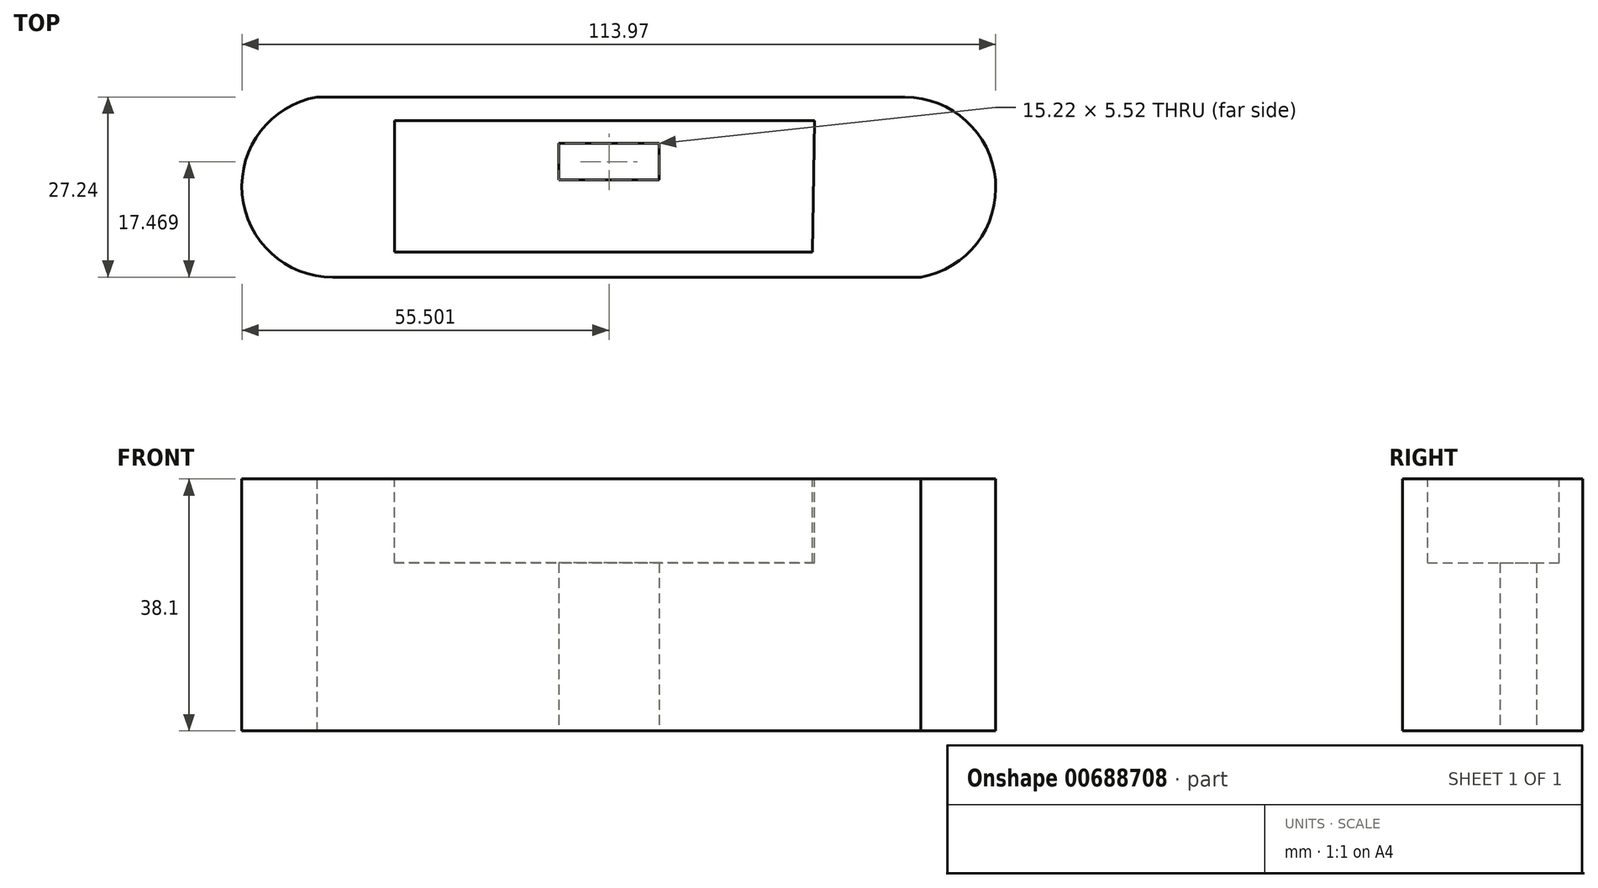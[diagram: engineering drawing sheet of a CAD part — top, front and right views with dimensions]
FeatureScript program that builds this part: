
annotation { "Feature Type Name" : "Feature", "Feature Type Description" : "" }
export const myFeature = defineFeature(function(context is Context, id is Id, definition is map)
    precondition{}
    {
        {
            var Q0;
            Q0=qCreatedBy(makeId("Top.planeOp"),FACE);
            var sketch = newSketch(context, id + "F0", { "sketchPlane" : qUnion([Q0])});
            skLineSegment(sketch, "E0", {"start": v(-44.14, 0) * mm, "end": v(44.76, 0) * mm});
            skArc(sketch, "E1", {"start": v(47.13, -27.24) * mm, "mid": v(58.43, -12.53) * mm, "end": v(44.76, 0) * mm});
            skLineSegment(sketch, "E2", {"start": v(47.13, -27.24) * mm, "end": v(-41.77, -27.24) * mm});
            skArc(sketch, "E3", {"start": v(-44.14, 0) * mm, "mid": v(-55.44, -14.71) * mm, "end": v(-41.77, -27.24) * mm});
            skSolve(sketch);
        }
        {
            var Q0;
            Q0=makeQuery(id+"F0.imprint","IMPRINT",FACE,{"disambiguationData":[TD([[makeQuery(id+"F0.imprint","IMPRINT",EDGE,{"derivedFrom":sQuery(id+"F0.wireOp",EDGE,"E0")}),-1.0]])]});
            extrude(context, id + "F1", {"entities" : qUnion([Q0]), "depth" : 12.7 * mm, "offsetDistance" : 25.4 * mm});
        }
        {
            var Q0;
            Q0=makeQuery(id+"F1.opExtrude","CAP_FACE",FACE,{"disambiguationData":[OSD([sQuery(id+"F0.wireOp",EDGE,"E0"),sQuery(id+"F0.wireOp",EDGE,"E1"),sQuery(id+"F0.wireOp",EDGE,"E2"),sQuery(id+"F0.wireOp",EDGE,"E3")])],"isStart":true});
            var sketch = newSketch(context, id + "F2", { "sketchPlane" : qUnion([Q0])});
            skLineSegment(sketch, "E4", {"start": v(-34.49, 27.24) * mm, "end": v(-34.49, 0) * mm});
            skSolve(sketch);
        }
        {
            var Q0;
            {var subQ0=sQuery(id+"F2.wireOp",EDGE,"E4");Q0=makeQuery(id+"F2.imprint","IMPRINT",FACE,{"disambiguationData":[TD([[makeQuery(id+"F2.imprint","IMPRINT",EDGE,{"derivedFrom":subQ0}),1.0]])]});}
            var sketch = newSketch(context, id + "F3", { "sketchPlane" : qUnion([Q0])});
            skLineSegment(sketch, "E5", {"start": v(31.5, 26.78) * mm, "end": v(31.5, 0) * mm});
            skSolve(sketch);
        }
        {
            var Q0;
            Q0 = qSketchRegion(id + "F3", true);
            var Q1;
            {var subQ0=sQuery(id+"F2.wireOp",EDGE,"E4");Q1=makeQuery(id+"F2.imprint","IMPRINT",FACE,{"disambiguationData":[TD([[makeQuery(id+"F2.imprint","IMPRINT",EDGE,{"derivedFrom":subQ0}),1.0]])]});}
            extrude(context, id + "F4", {"entities" : qUnion([Q0, Q1]), "operationType" : NewBodyOperationType.ADD, "depth" : 25.4 * mm, "offsetDistance" : 25.4 * mm});
        }
        {
            var Q0;
            Q0=makeQuery(id+"F1.opExtrude","CAP_FACE",FACE,{"disambiguationData":[OSD([sQuery(id+"F0.wireOp",EDGE,"E0"),sQuery(id+"F0.wireOp",EDGE,"E1"),sQuery(id+"F0.wireOp",EDGE,"E2"),sQuery(id+"F0.wireOp",EDGE,"E3")])],"isStart":true});
            extrude(context, id + "F5", {"entities" : qUnion([Q0]), "operationType" : NewBodyOperationType.ADD, "depth" : 25.4 * mm, "offsetDistance" : 25.4 * mm});
        }
        {
            var Q0;
            Q0=makeQuery(id+"F1.opExtrude","CAP_FACE",FACE,{"disambiguationData":[OSD([sQuery(id+"F0.wireOp",EDGE,"E0"),sQuery(id+"F0.wireOp",EDGE,"E1"),sQuery(id+"F0.wireOp",EDGE,"E2"),sQuery(id+"F0.wireOp",EDGE,"E3")])],"isStart":false});
            var sketch = newSketch(context, id + "F6", { "sketchPlane" : qUnion([Q0])});
            skLineSegment(sketch, "E6", {"start": v(31.07, -3.55) * mm, "end": v(-32.43, -3.55) * mm});
            skLineSegment(sketch, "E7", {"start": v(-32.43, -3.55) * mm, "end": v(-32.43, -23.47) * mm});
            skLineSegment(sketch, "E8", {"start": v(-32.43, -23.47) * mm, "end": v(30.79, -23.47) * mm});
            skLineSegment(sketch, "E9", {"start": v(30.79, -23.47) * mm, "end": v(31.07, -3.55) * mm});
            skSolve(sketch);
        }
        {
            var Q0;
            Q0 = qSketchRegion(id + "F6", true);
            extrude(context, id + "F7", {"entities" : qUnion([Q0]), "operationType" : NewBodyOperationType.REMOVE, "oppositeDirection" : true, "depth" : 12.7 * mm, "offsetDistance" : 25.4 * mm});
        }
        {
            var Q0;
            {var subQ0=sQuery(id+"F0.wireOp",EDGE,"E2");var subQ1=sQuery(id+"F0.wireOp",EDGE,"E1");var subQ2=sQuery(id+"F0.wireOp",EDGE,"E0");Q0=makeQuery(id+"F5.boolean.opBoolean","MERGE",FACE,{"derivedFrom":[makeQuery(id+"F4.opExtrude","CAP_FACE",FACE,{"disambiguationData":[OSD([subQ2,subQ1,subQ0,sQuery(id+"F2.wireOp",EDGE,"E4")])],"isStart":false}),makeQuery(id+"F5.opExtrude","CAP_FACE",FACE,{"disambiguationData":[OSD([subQ2,subQ1,subQ0,sQuery(id+"F0.wireOp",EDGE,"E3")])],"isStart":false})]});}
            var sketch = newSketch(context, id + "F8", { "sketchPlane" : qUnion([Q0])});
            skLineSegment(sketch, "E10", {"start": v(0, 12.53) * mm, "end": v(5.08, 12.53) * mm});
            skLineSegment(sketch, "E11", {"start": v(5.08, 12.53) * mm, "end": v(5.08, 7.01) * mm});
            skLineSegment(sketch, "E12", {"start": v(5.08, 7.01) * mm, "end": v(-5.06, 7.01) * mm});
            skLineSegment(sketch, "E13", {"start": v(-5.06, 7.01) * mm, "end": v(-5.06, 12.53) * mm});
            skPoint(sketch, "E13.endSnap0", {"position": v(2.54, 12.53) * mm});
            skLineSegment(sketch, "E14", {"start": v(-5.06, 12.53) * mm, "end": v(0, 12.53) * mm});
            skSolve(sketch);
        }
        {
            var Q0;
            Q0 = qSketchRegion(id + "F8", true);
            extrude(context, id + "F9", {"entities" : qUnion([Q0]), "operationType" : NewBodyOperationType.REMOVE, "oppositeDirection" : true, "depth" : 25.4 * mm, "offsetDistance" : 25.4 * mm});
        }
        {
            var Q0;
            {var subQ0=sQuery(id+"F0.wireOp",EDGE,"E2");var subQ1=sQuery(id+"F0.wireOp",EDGE,"E1");var subQ2=sQuery(id+"F0.wireOp",EDGE,"E0");Q0=makeQuery(id+"F5.boolean.opBoolean","MERGE",FACE,{"derivedFrom":[makeQuery(id+"F4.opExtrude","CAP_FACE",FACE,{"disambiguationData":[OSD([subQ2,subQ1,subQ0,sQuery(id+"F2.wireOp",EDGE,"E4")])],"isStart":false}),makeQuery(id+"F5.opExtrude","CAP_FACE",FACE,{"disambiguationData":[OSD([subQ2,subQ1,subQ0,sQuery(id+"F0.wireOp",EDGE,"E3")])],"isStart":false})]});}
            var sketch = newSketch(context, id + "F10", { "sketchPlane" : qUnion([Q0])});
            skLineSegment(sketch, "E15", {"start": v(-5.06, 12.53) * mm, "end": v(-7.6, 12.53) * mm});
            skLineSegment(sketch, "E16", {"start": v(-7.6, 12.53) * mm, "end": v(-7.6, 7.01) * mm});
            skLineSegment(sketch, "E17", {"start": v(-7.6, 7.01) * mm, "end": v(-5.06, 7.01) * mm});
            skLineSegment(sketch, "E18", {"start": v(-5.06, 7.01) * mm, "end": v(5.08, 7.01) * mm});
            skLineSegment(sketch, "E19", {"start": v(5.08, 7.01) * mm, "end": v(7.62, 7.01) * mm});
            skLineSegment(sketch, "E20", {"start": v(7.62, 7.01) * mm, "end": v(7.62, 12.53) * mm});
            skLineSegment(sketch, "E21", {"start": v(7.62, 12.53) * mm, "end": v(5.08, 12.53) * mm});
            skSolve(sketch);
        }
        {
            var Q0;
            Q0 = qSketchRegion(id + "F10", true);
            var Q1;
            Q1=makeQuery(id+"F10.imprint","IMPRINT",FACE,{"disambiguationData":[TD([[makeQuery(id+"F10.imprint","IMPRINT",EDGE,{"derivedFrom":sQuery(id+"F10.wireOp",EDGE,"E15")}),1.0]])]});
            var Q2;
            Q2=makeQuery(id+"F10.imprint","IMPRINT",FACE,{"disambiguationData":[TD([[makeQuery(id+"F10.imprint","IMPRINT",EDGE,{"derivedFrom":sQuery(id+"F10.wireOp",EDGE,"E19")}),1.0]])]});
            extrude(context, id + "F11", {"entities" : qUnion([Q0, Q1, Q2]), "operationType" : NewBodyOperationType.REMOVE, "oppositeDirection" : true, "depth" : 25.4 * mm, "offsetDistance" : 25.4 * mm});
        }
    });
